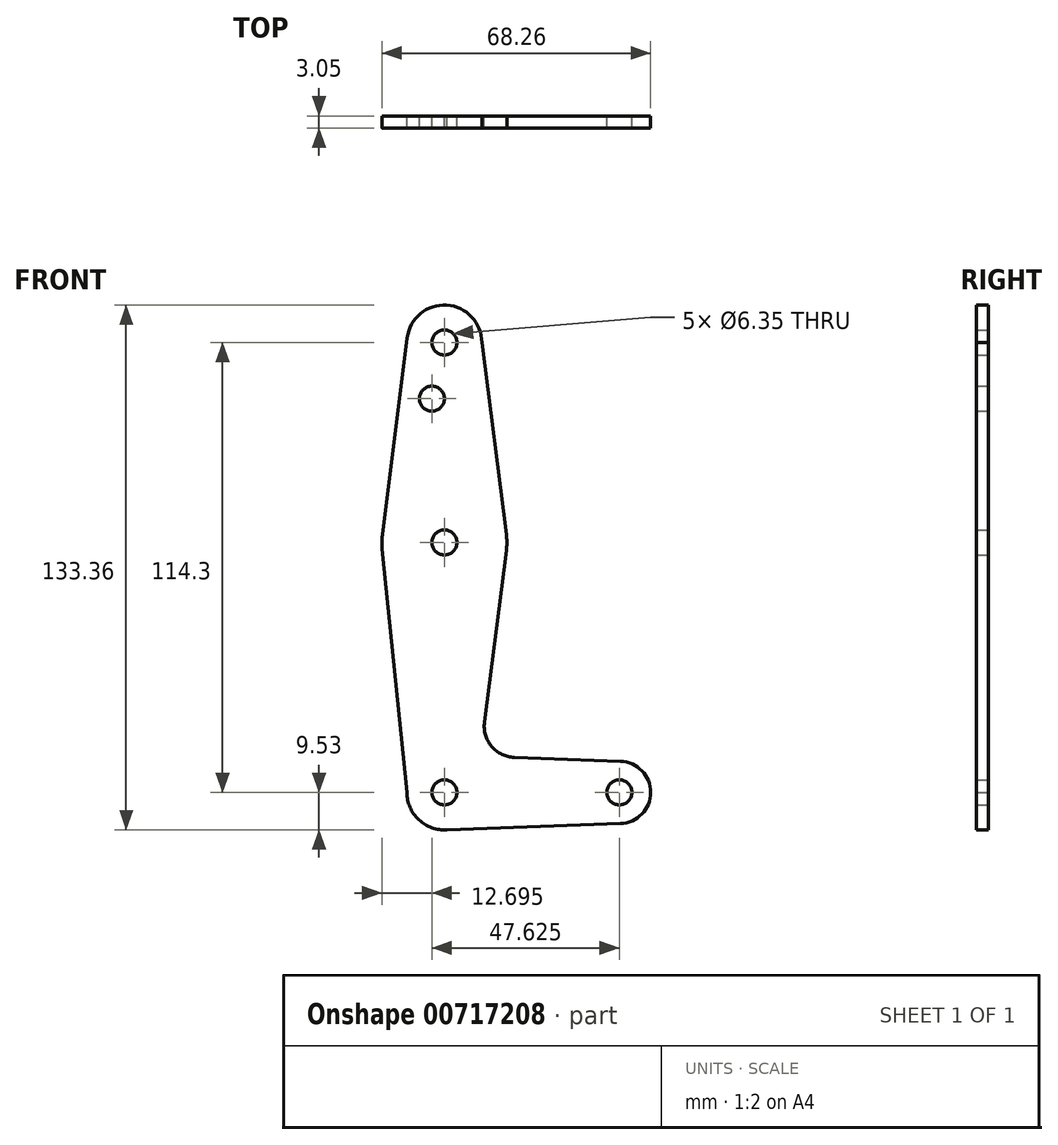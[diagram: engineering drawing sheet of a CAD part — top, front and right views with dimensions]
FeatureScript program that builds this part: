
annotation { "Feature Type Name" : "Feature", "Feature Type Description" : "" }
export const myFeature = defineFeature(function(context is Context, id is Id, definition is map)
    precondition{}
    {
        {
            var Q0;
            Q0=qCreatedBy(makeId("Front.planeOp"),FACE);
            var sketch = newSketch(context, id + "F0", { "sketchPlane" : qUnion([Q0])});
            skLineSegment(sketch, "E0", {"start": v(0, 0) * mm, "end": v(0, 63.5) * mm, "construction": true});
            skLineSegment(sketch, "E1", {"start": v(0, 63.5) * mm, "end": v(0, 114.3) * mm, "construction": true});
            skLineSegment(sketch, "E2", {"start": v(0, 0) * mm, "end": v(44.45, 0) * mm, "construction": true});
            skCircle(sketch, "E3", {"center": v(0, 114.3) * mm, "radius": 9.53 * mm});
            skCircle(sketch, "E4", {"center": v(0, 63.5) * mm, "radius": 15.88 * mm});
            skCircle(sketch, "E5", {"center": v(0, 0) * mm, "radius": 9.53 * mm});
            skCircle(sketch, "E6", {"center": v(44.45, 0) * mm, "radius": 7.94 * mm});
            skLineSegment(sketch, "E7", {"start": v(-9.45, 115.5) * mm, "end": v(-15.75, 65.48) * mm});
            skLineSegment(sketch, "E8", {"start": v(9.53, 114.3) * mm, "end": v(15.75, 65.5) * mm});
            skLineSegment(sketch, "E9", {"start": v(17.78, 8.9) * mm, "end": v(44.73, 7.93) * mm});
            skLineSegment(sketch, "E10", {"start": v(0, -9.53) * mm, "end": v(44.73, -7.93) * mm});
            skLineSegment(sketch, "E11", {"start": v(15.75, 61.5) * mm, "end": v(10.18, 17.84) * mm});
            skLineSegment(sketch, "E12", {"start": v(-9.53, 0) * mm, "end": v(-15.8, 61.9) * mm});
            skCircle(sketch, "E13", {"center": v(0, 114.3) * mm, "radius": 3.18 * mm});
            skCircle(sketch, "E14", {"center": v(0, 63.5) * mm, "radius": 3.18 * mm});
            skCircle(sketch, "E15", {"center": v(-3.18, 100.03) * mm, "radius": 3.18 * mm});
            skCircle(sketch, "E16", {"center": v(0, 0) * mm, "radius": 3.18 * mm});
            skCircle(sketch, "E17", {"center": v(44.45, 0) * mm, "radius": 3.18 * mm});
            skArc(sketch, "E18.filletArc", {"start": v(10.18, 17.84) * mm, "mid": v(12, 11.69) * mm, "end": v(17.78, 8.9) * mm});
            skSolve(sketch);
        }
        {
            var Q0;
            Q0 = qSketchRegion(id + "F0", true);
            extrude(context, id + "F1", {"entities" : qUnion([Q0]), "depth" : 3.05 * mm, "offsetDistance" : 25.4 * mm});
        }
    });
